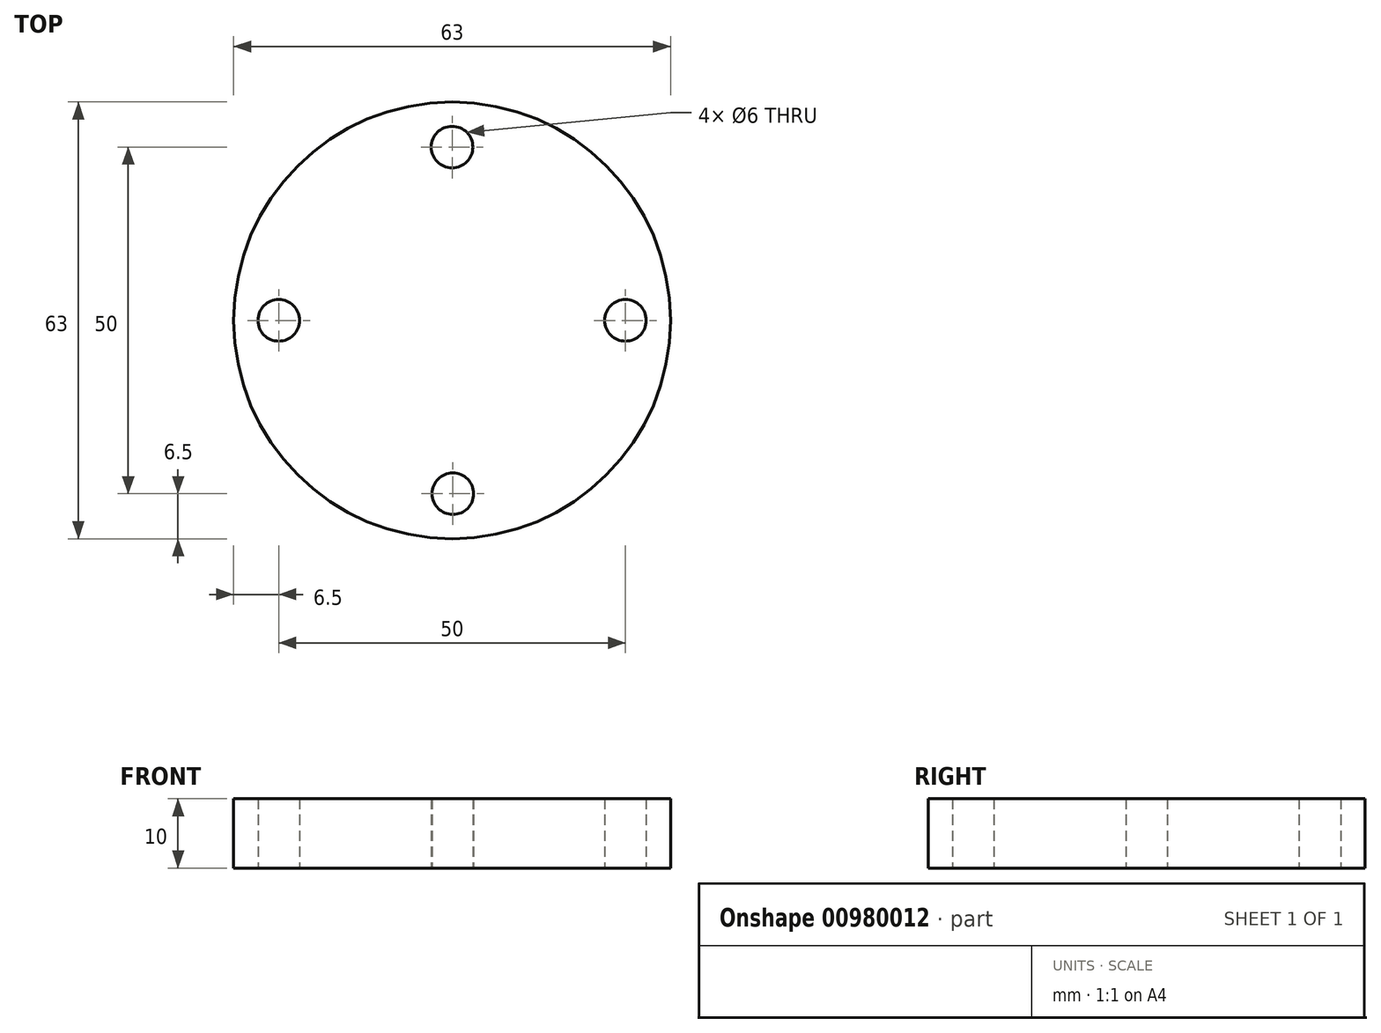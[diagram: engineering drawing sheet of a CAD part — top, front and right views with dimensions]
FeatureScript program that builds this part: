
annotation { "Feature Type Name" : "Feature", "Feature Type Description" : "" }
export const myFeature = defineFeature(function(context is Context, id is Id, definition is map)
    precondition{}
    {
        {
            var Q0;
            Q0=qCreatedBy(makeId("Top.planeOp"),FACE);
            var sketch = newSketch(context, id + "F0", { "sketchPlane" : qUnion([Q0])});
            skCircle(sketch, "E0", {"center": v(0, 0) * mm, "radius": 31.5 * mm});
            skCircle(sketch, "E1", {"center": v(0, 0) * mm, "radius": 25 * mm, "construction": true});
            skPoint(sketch, "E2", {"position": v(-25, 0) * mm});
            skPoint(sketch, "E3", {"position": v(0, 25) * mm});
            skPoint(sketch, "E4", {"position": v(25, 0) * mm});
            skPoint(sketch, "E5", {"position": v(0.1, -25) * mm});
            skCircle(sketch, "E6", {"center": v(0, 25) * mm, "radius": 3 * mm});
            skCircle(sketch, "E7", {"center": v(25, 0) * mm, "radius": 3 * mm});
            skCircle(sketch, "E8", {"center": v(0.1, -25) * mm, "radius": 3 * mm});
            skCircle(sketch, "E9", {"center": v(-25, 0) * mm, "radius": 3 * mm});
            skSolve(sketch);
        }
        {
            var Q0;
            Q0=makeQuery(id+"F0.imprint","IMPRINT",FACE,{"disambiguationData":[TD([[makeQuery(id+"F0.imprint","IMPRINT",EDGE,{"derivedFrom":sQuery(id+"F0.wireOp",EDGE,"E0")}),1.0]])]});
            extrude(context, id + "F1", {"entities" : qUnion([Q0]), "depth" : 10 * mm, "offsetDistance" : 25 * mm});
        }
    });
